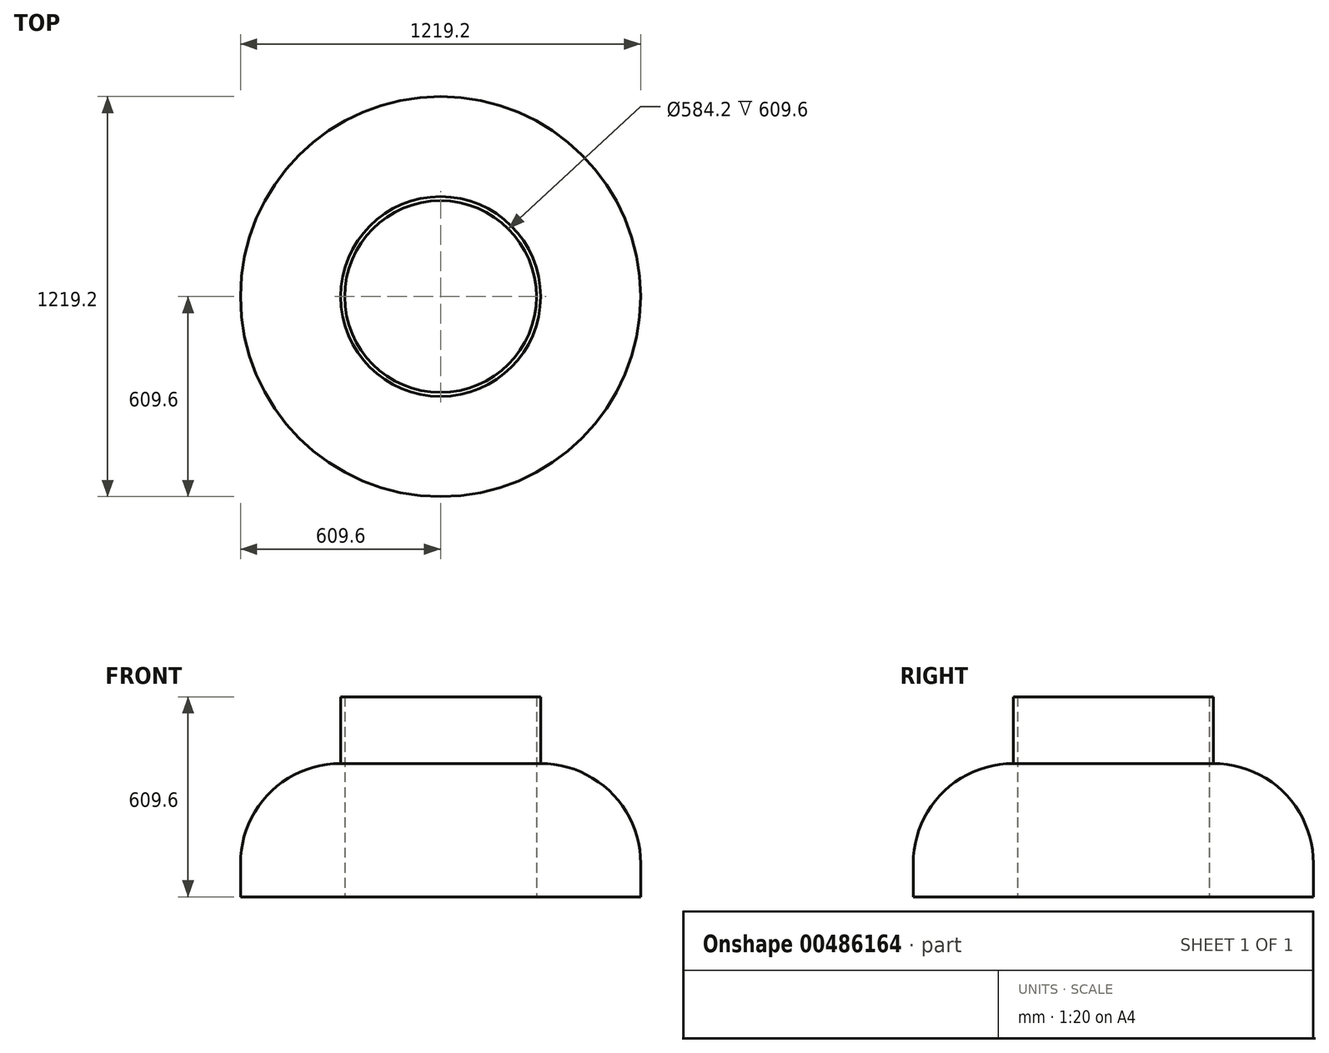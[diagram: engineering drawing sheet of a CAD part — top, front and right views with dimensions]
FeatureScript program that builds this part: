
annotation { "Feature Type Name" : "Feature", "Feature Type Description" : "" }
export const myFeature = defineFeature(function(context is Context, id is Id, definition is map)
    precondition{}
    {
        {
            var Q0;
            Q0=qCreatedBy(makeId("Top.planeOp"),FACE);
            var sketch = newSketch(context, id + "F0", { "sketchPlane" : qUnion([Q0])});
            skCircle(sketch, "E0", {"center": v(0, 0) * mm, "radius": 609.6 * mm});
            skCircle(sketch, "E1", {"center": v(0, 0) * mm, "radius": 304.8 * mm});
            skSolve(sketch);
        }
        {
            var Q0;
            Q0 = qSketchRegion(id + "F0", true);
            extrude(context, id + "F1", {"entities" : qUnion([Q0]), "depth" : 406.4 * mm});
        }
        {
            var Q0;
            Q0=makeQuery(id+"F1.opExtrude","CAP_EDGE",EDGE,{"disambiguationData":[OSD([sQuery(id+"F0.wireOp",EDGE,"E0")])],"isStart":false});
            fillet(context, id + "F2", {"entities" : qUnion([Q0]), "radius" : 304.8 * mm, "tangentPropagation" : true, "allowEdgeOverflow" : false});
        }
        {
            var Q0;
            Q0=qCreatedBy(makeId("Top.planeOp"),FACE);
            var sketch = newSketch(context, id + "F3", { "sketchPlane" : qUnion([Q0])});
            skCircle(sketch, "E2", {"center": v(0, 0) * mm, "radius": 304.8 * mm});
            skCircle(sketch, "E3", {"center": v(0, 0) * mm, "radius": 292.1 * mm});
            skSolve(sketch);
        }
        {
            var Q0;
            Q0 = qSketchRegion(id + "F3", true);
            extrude(context, id + "F4", {"entities" : qUnion([Q0]), "operationType" : NewBodyOperationType.ADD, "depth" : 609.6 * mm});
        }
    });
